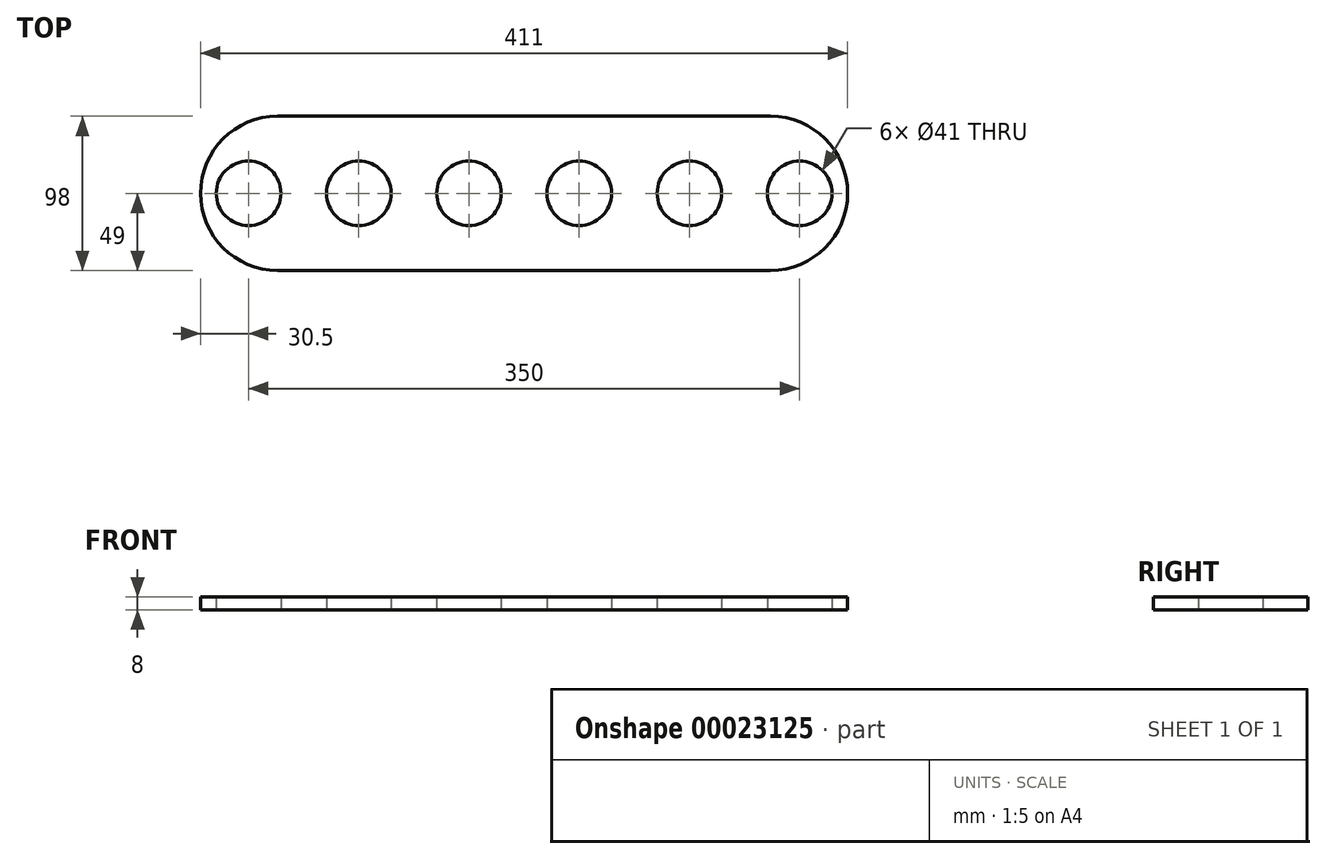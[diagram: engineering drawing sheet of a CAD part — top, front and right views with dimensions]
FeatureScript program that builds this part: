
annotation { "Feature Type Name" : "Feature", "Feature Type Description" : "" }
export const myFeature = defineFeature(function(context is Context, id is Id, definition is map)
    precondition{}
    {
        {
            var Q0;
            Q0=qCreatedBy(makeId("Top.planeOp"),FACE);
            var sketch = newSketch(context, id + "F0", { "sketchPlane" : qUnion([Q0])});
            skLineSegment(sketch, "E0.rect.bottom", {"start": v(-156.5, -49) * mm, "end": v(156.5, -49) * mm});
            skLineSegment(sketch, "E0.rect.top", {"start": v(-156.5, 49) * mm, "end": v(156.5, 49) * mm});
            skPoint(sketch, "E0.rect.middle", {"position": v(0, 0) * mm});
            skArc(sketch, "E1", {"start": v(-156.5, 49) * mm, "mid": v(-205.5, 0) * mm, "end": v(-156.5, -49) * mm});
            skArc(sketch, "E2", {"start": v(156.5, -49) * mm, "mid": v(205.5, 0) * mm, "end": v(156.5, 49) * mm});
            skCircle(sketch, "E3", {"center": v(35, 0) * mm, "radius": 20.5 * mm});
            skCircle(sketch, "E4", {"center": v(105, 0) * mm, "radius": 20.5 * mm});
            skCircle(sketch, "E5", {"center": v(175, 0) * mm, "radius": 20.5 * mm});
            skCircle(sketch, "E6", {"center": v(-35, 0) * mm, "radius": 20.5 * mm});
            skCircle(sketch, "E7", {"center": v(-105, 0) * mm, "radius": 20.5 * mm});
            skCircle(sketch, "E8", {"center": v(-175, 0) * mm, "radius": 20.5 * mm});
            skSolve(sketch);
        }
        {
            var Q0;
            Q0 = qSketchRegion(id + "F0", true);
            extrude(context, id + "F1", {"entities" : qUnion([Q0]), "depth" : 8 * mm});
        }
    });
